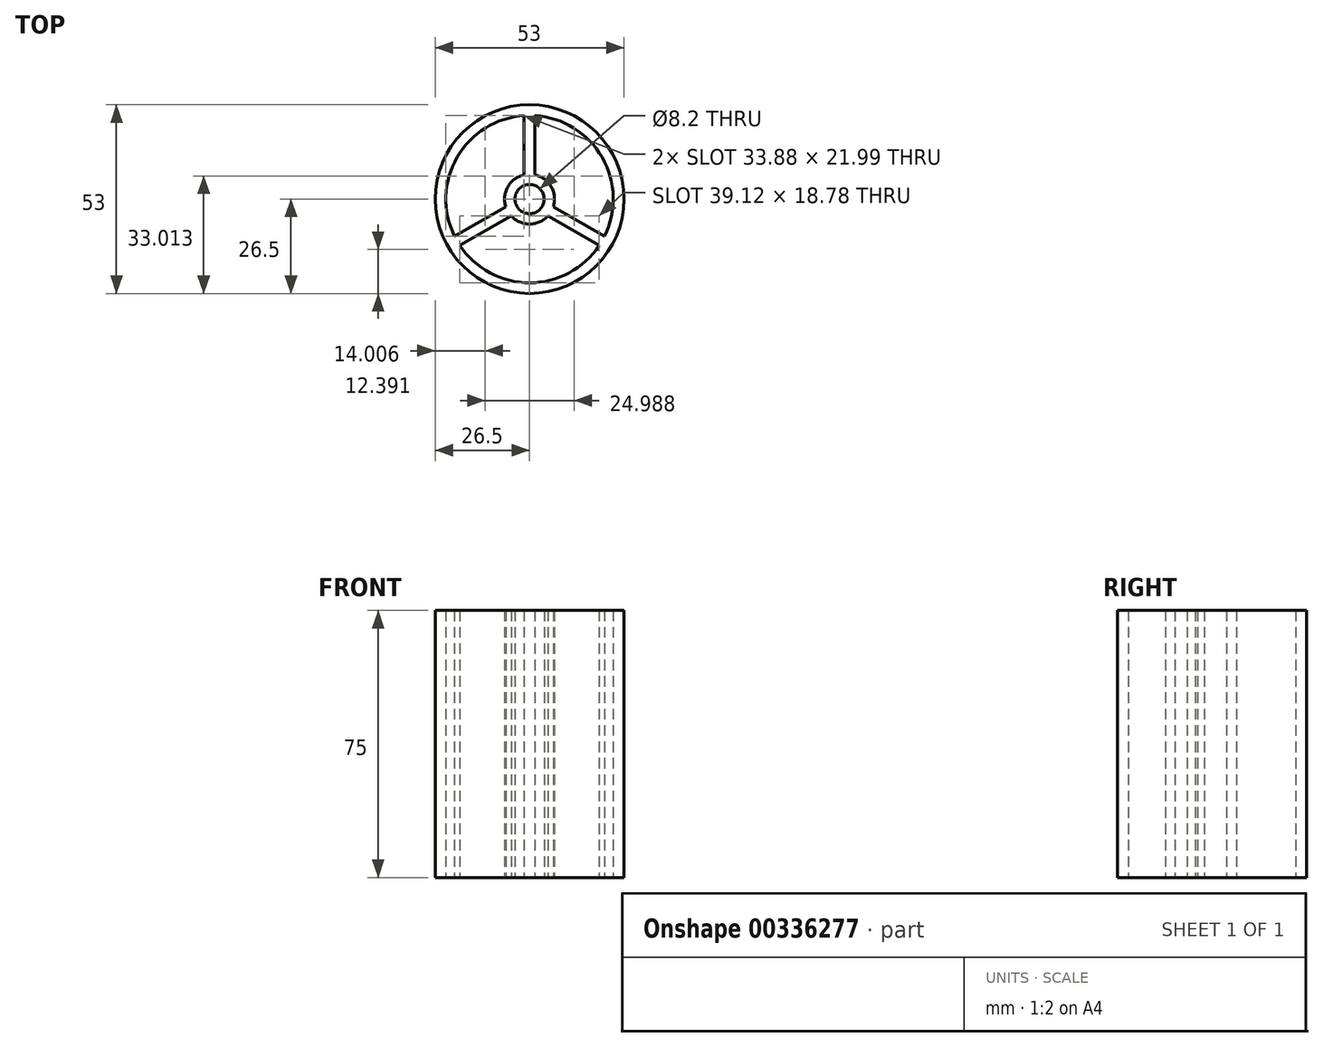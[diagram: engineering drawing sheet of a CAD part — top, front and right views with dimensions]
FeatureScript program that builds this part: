
annotation { "Feature Type Name" : "Feature", "Feature Type Description" : "" }
export const myFeature = defineFeature(function(context is Context, id is Id, definition is map)
    precondition{}
    {
        {
            var Q0;
            Q0=qCreatedBy(makeId("Top.planeOp"),FACE);
            var sketch = newSketch(context, id + "F0", { "sketchPlane" : qUnion([Q0])});
            skCircle(sketch, "E0", {"center": v(0, 0) * mm, "radius": 26.5 * mm});
            skCircle(sketch, "E1", {"center": v(0, 0) * mm, "radius": 4.1 * mm});
            skCircle(sketch, "E2", {"center": v(0, 0) * mm, "radius": 7 * mm});
            skCircle(sketch, "E3", {"center": v(0, 0) * mm, "radius": 23.5 * mm});
            skLineSegment(sketch, "E4", {"start": v(0, 7) * mm, "end": v(0, 23.5) * mm});
            skLineSegment(sketch, "E5", {"start": v(1.5, 23.45) * mm, "end": v(1.5, 6.84) * mm});
            skLineSegment(sketch, "E6", {"start": v(-1.5, 6.84) * mm, "end": v(-1.5, 23.45) * mm});
            skLineSegment(sketch, "E7.1.0", {"start": v(-5.17, -4.72) * mm, "end": v(-19.56, -13.03) * mm});
            skLineSegment(sketch, "E7.1.1", {"start": v(-21.06, -10.43) * mm, "end": v(-6.67, -2.12) * mm});
            skLineSegment(sketch, "E7.2.0", {"start": v(6.67, -2.12) * mm, "end": v(21.06, -10.43) * mm});
            skLineSegment(sketch, "E7.2.1", {"start": v(19.56, -13.03) * mm, "end": v(5.17, -4.72) * mm});
            skSolve(sketch);
        }
        {
            var Q0;
            Q0=makeQuery(id+"F0.imprint","IMPRINT",FACE,{"disambiguationData":[TD([[makeQuery(id+"F0.imprint","IMPRINT",EDGE,{"derivedFrom":sQuery(id+"F0.wireOp",EDGE,"E0")}),1.0]])]});
            var Q1;
            {var subQ0=sQuery(id+"F0.wireOp",EDGE,"E4");Q1=makeQuery(id+"F0.imprint","IMPRINT",FACE,{"disambiguationData":[TD([[makeQuery(id+"F0.imprint","IMPRINT",EDGE,{"derivedFrom":subQ0}),1.0]])]});}
            var Q2;
            {var subQ0=sQuery(id+"F0.wireOp",EDGE,"E4");Q2=makeQuery(id+"F0.imprint","IMPRINT",FACE,{"disambiguationData":[TD([[makeQuery(id+"F0.imprint","IMPRINT",EDGE,{"derivedFrom":subQ0}),-1.0]])]});}
            var Q3;
            {var subQ0=sQuery(id+"F0.wireOp",EDGE,"E7.2.0");Q3=makeQuery(id+"F0.imprint","IMPRINT",FACE,{"disambiguationData":[TD([[makeQuery(id+"F0.imprint","IMPRINT",EDGE,{"derivedFrom":subQ0}),-1.0]])]});}
            var Q4;
            Q4=makeQuery(id+"F0.imprint","IMPRINT",FACE,{"disambiguationData":[TD([[makeQuery(id+"F0.imprint","IMPRINT",EDGE,{"derivedFrom":sQuery(id+"F0.wireOp",EDGE,"E1")}),-1.0]])]});
            var Q5;
            {var subQ0=sQuery(id+"F0.wireOp",EDGE,"E7.1.0");Q5=makeQuery(id+"F0.imprint","IMPRINT",FACE,{"disambiguationData":[TD([[makeQuery(id+"F0.imprint","IMPRINT",EDGE,{"derivedFrom":subQ0}),-1.0]])]});}
            extrude(context, id + "F1", {"entities" : qUnion([Q0, Q1, Q2, Q3, Q4, Q5]), "depth" : 75 * mm});
        }
    });
